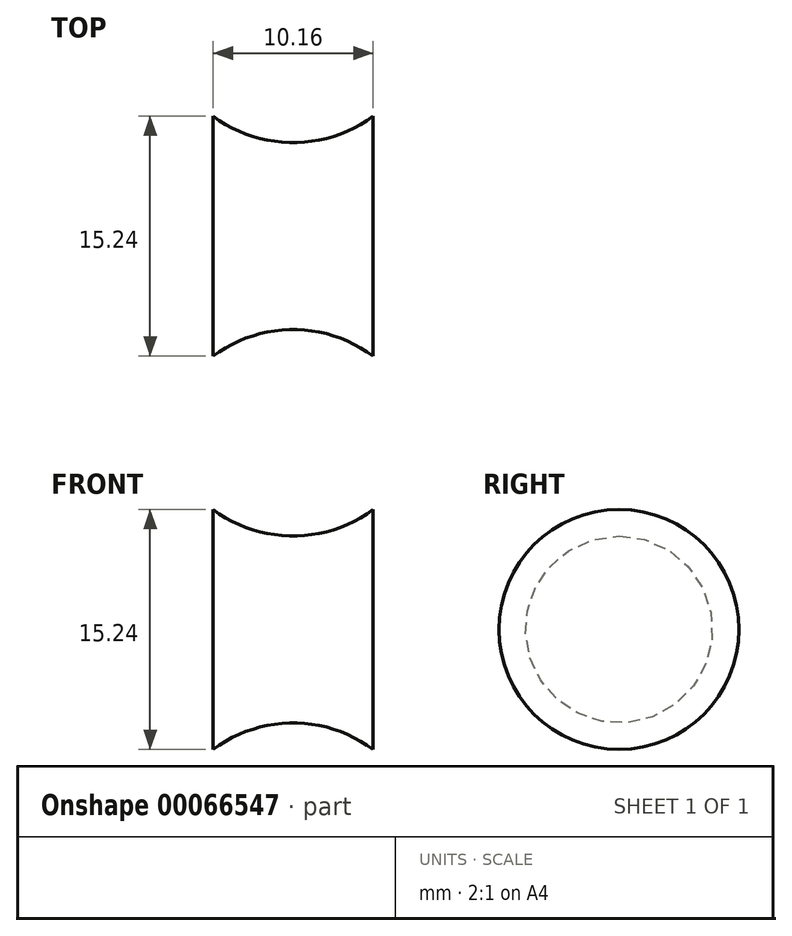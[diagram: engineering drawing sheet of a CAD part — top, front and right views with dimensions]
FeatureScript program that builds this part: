
annotation { "Feature Type Name" : "Feature", "Feature Type Description" : "" }
export const myFeature = defineFeature(function(context is Context, id is Id, definition is map)
    precondition{}
    {
        {
            var Q0;
            Q0=qCreatedBy(makeId("Top.planeOp"),FACE);
            var sketch = newSketch(context, id + "F0", { "sketchPlane" : qUnion([Q0])});
            skLineSegment(sketch, "E0", {"start": v(-8.96, -21.33) * mm, "end": v(1.2, -21.33) * mm, "construction": true});
            skArc(sketch, "E1", {"start": v(-8.96, -21.33) * mm, "mid": v(-3.88, -23.02) * mm, "end": v(1.2, -21.33) * mm});
            skLineSegment(sketch, "E2", {"start": v(-8.96, -21.33) * mm, "end": v(-8.96, -28.95) * mm});
            skLineSegment(sketch, "E3", {"start": v(1.2, -21.33) * mm, "end": v(1.2, -28.95) * mm});
            skLineSegment(sketch, "E4", {"start": v(-8.96, -28.95) * mm, "end": v(1.2, -28.95) * mm});
            skSolve(sketch);
        }
        {
            var Q0;
            Q0=qSketchRegion(id+"F0",true);
            var Q1;
            Q1=sQuery(id+"F0.wireOp",EDGE,"E4");
            revolve(context, id + "F1", {"entities" : qUnion([Q0]), "axis" : qUnion([Q1]), "revolveType" : RevolveType.FULL});
        }
    });
